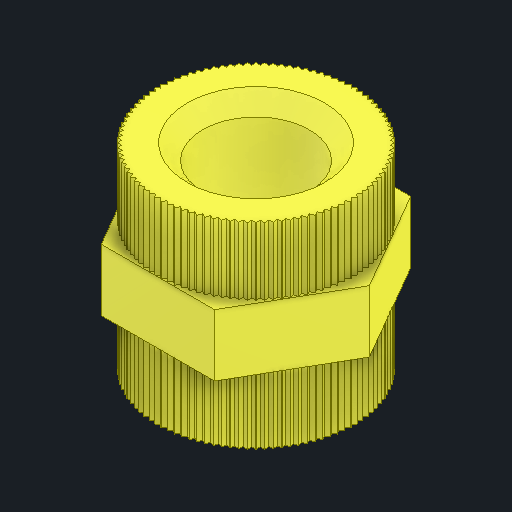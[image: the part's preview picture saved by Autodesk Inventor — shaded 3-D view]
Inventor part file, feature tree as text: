
AUTODESK INVENTOR PART (.ipt)
format: ipt  version: 2024 (Build 280153000, 153)  size: 615,424 bytes
history: native  units: in
note: dims shown in document units (in); Inventor stores cm internally (conversion verified against a paired STEP export)
features: chamfer x1
ambient origin geometry x8: Origin, YZ Plane, XZ Plane, XY Plane, X Axis, Y Axis, Z Axis, Center Point
bodies: Solid1 (feature_tree)
feature tree (1):
  chamfer  "Chamfer1"  [1 undecoded]
note: 1 required parameter value undecoded (feature->parameter linkage not recoverable at this tier; creation-order binding heuristic only, values carry confidence <= 0.55)
